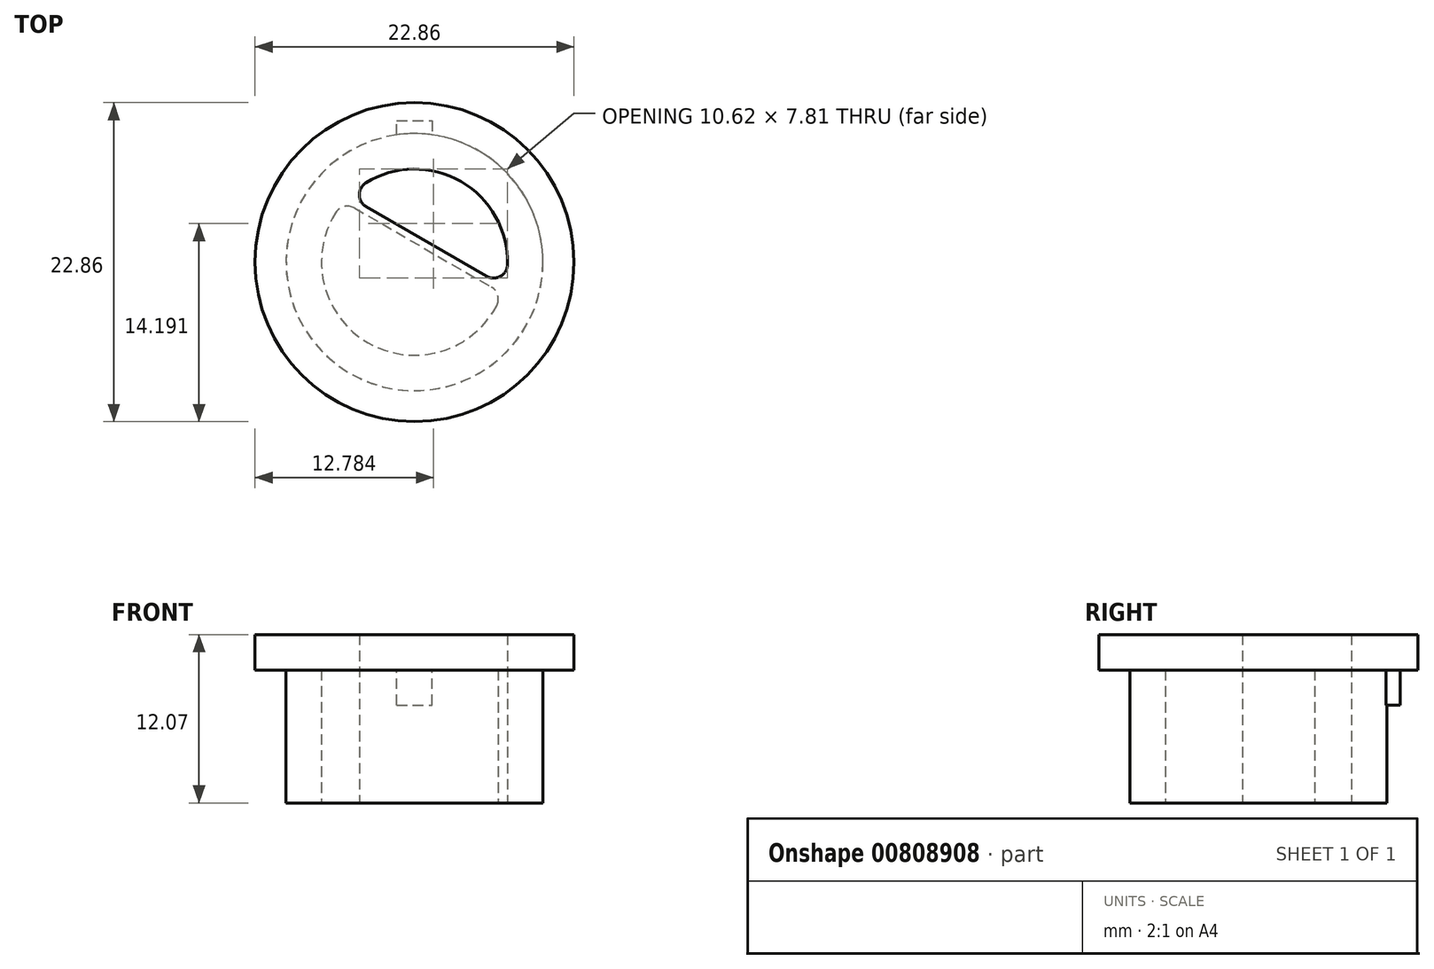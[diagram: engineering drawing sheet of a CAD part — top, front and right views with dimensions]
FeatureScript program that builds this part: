
annotation { "Feature Type Name" : "Feature", "Feature Type Description" : "" }
export const myFeature = defineFeature(function(context is Context, id is Id, definition is map)
    precondition{}
    {
        {
            var Q0;
            Q0=qCreatedBy(makeId("Top.planeOp"),FACE);
            var sketch = newSketch(context, id + "F0", { "sketchPlane" : qUnion([Q0])});
            skCircle(sketch, "E0", {"center": v(0, 0) * mm, "radius": 9.2 * mm});
            skCircle(sketch, "E1", {"center": v(0, 0) * mm, "radius": 6.67 * mm});
            skLineSegment(sketch, "E2", {"start": v(-4.73, 4.7) * mm, "end": v(6.44, -1.74) * mm});
            skLineSegment(sketch, "E3", {"start": v(-5.07, 4.32) * mm, "end": v(6.28, -2.23) * mm});
            skCircle(sketch, "E4.cCircle", {"center": v(0, 0) * mm, "radius": 5.77 * mm, "construction": true});
            skLineSegment(sketch, "E4.0", {"start": v(0, 6.67) * mm, "end": v(5.77, 3.33) * mm, "construction": true});
            skLineSegment(sketch, "E4.1", {"start": v(5.77, 3.33) * mm, "end": v(5.77, -3.33) * mm, "construction": true});
            skLineSegment(sketch, "E4.2", {"start": v(5.77, -3.33) * mm, "end": v(0, -6.67) * mm, "construction": true});
            skLineSegment(sketch, "E4.3", {"start": v(0, -6.67) * mm, "end": v(-5.77, -3.33) * mm, "construction": true});
            skLineSegment(sketch, "E4.4", {"start": v(-5.77, -3.33) * mm, "end": v(-5.77, 3.33) * mm, "construction": true});
            skLineSegment(sketch, "E4.5", {"start": v(-5.77, 3.33) * mm, "end": v(0, 6.67) * mm, "construction": true});
            skPoint(sketch, "E4.0.midPoint", {"position": v(2.89, 5) * mm});
            skSolve(sketch);
        }
        {
            var Q0;
            Q0 = qSketchRegion(id + "F0", true);
            var Q1;
            {var subQ0=sQuery(id+"F0.wireOp",EDGE,"E2");Q1=makeQuery(id+"F0.imprint","IMPRINT",FACE,{"disambiguationData":[TD([[makeQuery(id+"F0.imprint","IMPRINT",EDGE,{"derivedFrom":subQ0}),-1.0]])]});}
            extrude(context, id + "F1", {"entities" : qUnion([Q0, Q1]), "depth" : 9.52 * mm, "offsetDistance" : 25 * mm});
        }
        {
            var Q0;
            Q0=makeQuery(id+"F1.opExtrude","CAP_FACE",FACE,{"disambiguationData":[OSD([sQuery(id+"F0.wireOp",EDGE,"E0"),sQuery(id+"F0.wireOp",EDGE,"E1"),sQuery(id+"F0.wireOp",EDGE,"E2"),sQuery(id+"F0.wireOp",EDGE,"E3")])],"isStart":false});
            var sketch = newSketch(context, id + "F2", { "sketchPlane" : qUnion([Q0])});
            skCircle(sketch, "E5", {"center": v(0, 0) * mm, "radius": 11.43 * mm});
            skArc(sketch, "E6.0", {"start": v(6.44, -1.74) * mm, "mid": v(3.33, 5.77) * mm, "end": v(-4.73, 4.7) * mm});
            skLineSegment(sketch, "E6.1", {"start": v(-4.73, 4.7) * mm, "end": v(6.44, -1.74) * mm});
            skSolve(sketch);
        }
        {
            var Q0;
            Q0 = qSketchRegion(id + "F2", true);
            extrude(context, id + "F3", {"entities" : qUnion([Q0]), "operationType" : NewBodyOperationType.ADD, "depth" : 2.54 * mm, "offsetDistance" : 25 * mm});
        }
        {
            var Q0;
            {var subQ0=sQuery(id+"F2.wireOp",EDGE,"E5");Q0=makeQuery(id+"F3.boolean.opBoolean","SPLIT",FACE,{"disambiguationData":[TD([makeQuery(id+"F1.opExtrude","SWEPT_FACE",FACE,{"disambiguationData":[OSD([sQuery(id+"F0.wireOp",EDGE,"E0")])]})])],"derivedFrom":makeQuery(id+"F3.opExtrude","CAP_FACE",FACE,{"disambiguationData":[OSD([subQ0,sQuery(id+"F2.wireOp",EDGE,"E6.0"),sQuery(id+"F2.wireOp",EDGE,"E6.1")])],"isStart":true})});}
            var sketch = newSketch(context, id + "F4", { "sketchPlane" : qUnion([Q0])});
            skLineSegment(sketch, "E7", {"start": v(-1.27, -9.12) * mm, "end": v(-1.27, -10.14) * mm});
            skLineSegment(sketch, "E8", {"start": v(-1.27, -10.14) * mm, "end": v(1.27, -10.14) * mm});
            skLineSegment(sketch, "E9", {"start": v(1.27, -10.14) * mm, "end": v(1.27, -9.12) * mm});
            skLineSegment(sketch, "E10", {"start": v(1.27, -9.12) * mm, "end": v(-1.27, -9.12) * mm});
            skLineSegment(sketch, "E11", {"start": v(0, -10.14) * mm, "end": v(0, -6.67) * mm, "construction": true});
            skSolve(sketch);
        }
        {
            var Q0;
            Q0 = qSketchRegion(id + "F4", true);
            extrude(context, id + "F5", {"entities" : qUnion([Q0]), "operationType" : NewBodyOperationType.ADD, "depth" : 2.5 * mm, "offsetDistance" : 25 * mm});
        }
        {
            var Q0;
            {var subQ0=sQuery(id+"F2.wireOp",EDGE,"E6.1");var subQ1=sQuery(id+"F2.wireOp",EDGE,"E6.0");var subQ2=sQuery(id+"F0.wireOp",EDGE,"E2");var subQ3=sQuery(id+"F0.wireOp",EDGE,"E1");Q0=makeQuery(id+"F3.boolean.opBoolean","MERGE",EDGE,{"derivedFrom":[makeQuery(id+"F1.opExtrude","SWEPT_EDGE",EDGE,{"disambiguationData":[OSD([subQ3,subQ2]),TDD([makeQuery(id+"F0.imprint","INTERSECT",VERTEX,{"disambiguationData":[OD(1.0)],"derivedFrom":[subQ3,subQ2]})])]}),makeQuery(id+"F3.opExtrude","SWEPT_EDGE",EDGE,{"disambiguationData":[OSD([subQ1,subQ0]),TDD([makeQuery(id+"F2.imprint","INTERSECT",VERTEX,{"disambiguationData":[OD(1.0)],"derivedFrom":[subQ1,subQ0]})])]})]});}
            var Q1;
            {var subQ0=sQuery(id+"F2.wireOp",EDGE,"E6.1");var subQ1=sQuery(id+"F2.wireOp",EDGE,"E6.0");var subQ2=sQuery(id+"F0.wireOp",EDGE,"E2");var subQ3=sQuery(id+"F0.wireOp",EDGE,"E1");Q1=makeQuery(id+"F3.boolean.opBoolean","MERGE",EDGE,{"derivedFrom":[makeQuery(id+"F1.opExtrude","SWEPT_EDGE",EDGE,{"disambiguationData":[OSD([subQ3,subQ2]),TDD([makeQuery(id+"F0.imprint","INTERSECT",VERTEX,{"disambiguationData":[OD(0.0)],"derivedFrom":[subQ3,subQ2]})])]}),makeQuery(id+"F3.opExtrude","SWEPT_EDGE",EDGE,{"disambiguationData":[OSD([subQ1,subQ0]),TDD([makeQuery(id+"F2.imprint","INTERSECT",VERTEX,{"disambiguationData":[OD(0.0)],"derivedFrom":[subQ1,subQ0]})])]})]});}
            var Q2;
            {var subQ0=sQuery(id+"F0.wireOp",EDGE,"E3");var subQ1=sQuery(id+"F0.wireOp",EDGE,"E1");Q2=makeQuery(id+"F1.opExtrude","SWEPT_EDGE",EDGE,{"disambiguationData":[OSD([subQ1,subQ0]),TDD([makeQuery(id+"F0.imprint","INTERSECT",VERTEX,{"disambiguationData":[OD(0.0)],"derivedFrom":[subQ1,subQ0]})])]});}
            var Q3;
            {var subQ0=sQuery(id+"F0.wireOp",EDGE,"E3");var subQ1=sQuery(id+"F0.wireOp",EDGE,"E1");Q3=makeQuery(id+"F1.opExtrude","SWEPT_EDGE",EDGE,{"disambiguationData":[OSD([subQ1,subQ0]),TDD([makeQuery(id+"F0.imprint","INTERSECT",VERTEX,{"disambiguationData":[OD(1.0)],"derivedFrom":[subQ1,subQ0]})])]});}
            fillet(context, id + "F6", {"entities" : qUnion([Q0, Q1, Q2, Q3]), "radius" : 1 * mm, "tangentPropagation" : true, "allowEdgeOverflow" : false});
        }
    });
